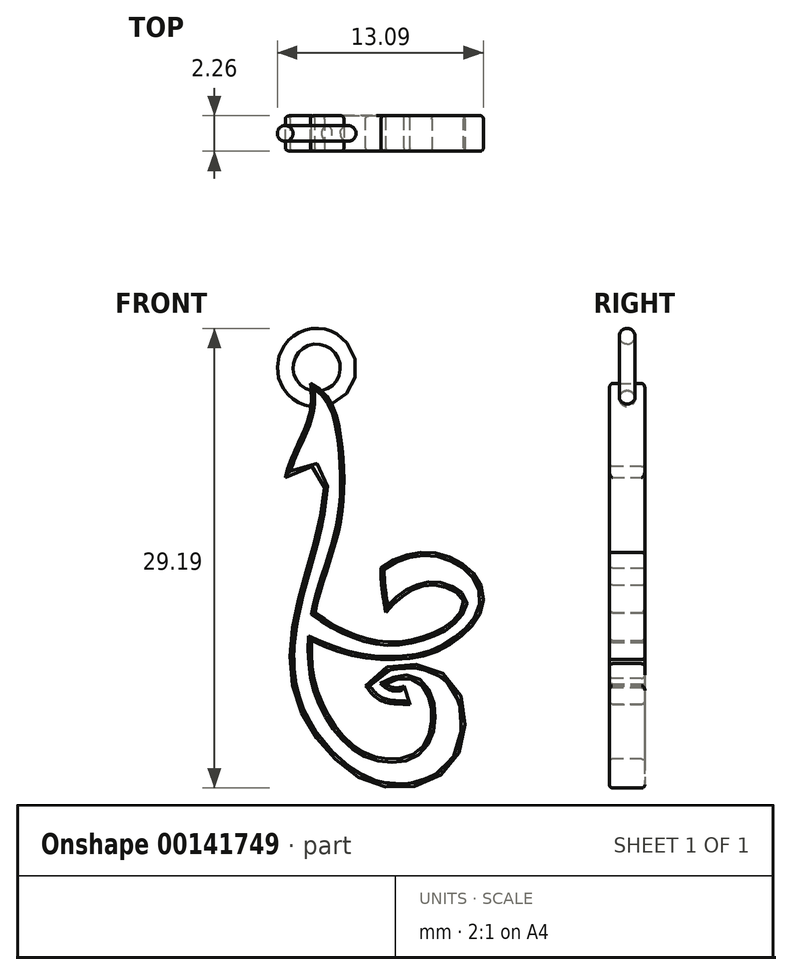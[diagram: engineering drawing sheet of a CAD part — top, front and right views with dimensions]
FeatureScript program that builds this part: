
annotation { "Feature Type Name" : "Feature", "Feature Type Description" : "" }
export const myFeature = defineFeature(function(context is Context, id is Id, definition is map)
    precondition{}
    {
        {
            var Q0;
            Q0=qCreatedBy(makeId("Front.planeOp"),FACE);
            var sketch = newSketch(context, id + "F0", { "sketchPlane" : qUnion([Q0])});
            skLineSegment(sketch, "E0.bottom", {"start": v(-7.5, 0) * mm, "end": v(9.5, 0) * mm, "construction": true});
            skLineSegment(sketch, "E0.top", {"start": v(-7.5, 17) * mm, "end": v(9.5, 17) * mm, "construction": true});
            skLineSegment(sketch, "E0.left", {"start": v(-7.5, 0) * mm, "end": v(-7.5, 17) * mm, "construction": true});
            skLineSegment(sketch, "E0.right", {"start": v(9.5, 0) * mm, "end": v(9.5, 17) * mm, "construction": true});
            skLineSegment(sketch, "E1", {"start": v(0, 0) * mm, "end": v(0, 23.23) * mm, "construction": true});
            skLineSegment(sketch, "E2", {"start": v(2.11, 3.42) * mm, "end": v(1.86, 4.2) * mm});
            skFitSpline(sketch, "E3", {"points": [v(1.86, 4.2) * mm, v(1.1, 4.27) * mm], "startDerivative": vector(-0.68, -0.46) * mm, "endDerivative": vector(-0.68, 0.54) * mm});
            skFitSpline(sketch, "E4", {"points": [v(1.1, 4.27) * mm, v(1.6, 4.48) * mm, v(2.23, 4.46) * mm, v(2.83, 3.93) * mm, v(3.04, 2.91) * mm, v(2.87, 1.98) * mm, v(2.32, 1.32) * mm, v(1.42, 1.1) * mm, v(0.23, 1.34) * mm, v(-0.95, 2.35) * mm, v(-1.8, 3.96) * mm, v(-2.06, 5.52) * mm, v(-1.91, 7.29) * mm, v(-1.38, 9.13) * mm, v(-0.76, 11.56) * mm, v(-0.75, 14.1) * mm, v(-1.06, 15.82) * mm, v(-1.44, 16.5) * mm, v(-2.1, 17) * mm], "startDerivative": vector(23.92, 10.43) * mm, "endDerivative": vector(-24, 9.9) * mm});
            skFitSpline(sketch, "E5", {"points": [v(-1.91, 7.29) * mm, v(-0.55, 6.48) * mm, v(1.22, 6.04) * mm, v(2.68, 6.28) * mm, v(3.76, 6.8) * mm, v(4.4, 7.67) * mm, v(4.1, 8.14) * mm, v(3.43, 8.42) * mm, v(2.66, 8.42) * mm, v(1.7, 7.91) * mm, v(1.1, 7.3) * mm], "startDerivative": vector(12.7, -8.61) * mm, "endDerivative": vector(-6.05, -7.17) * mm});
            skFitSpline(sketch, "E6", {"points": [v(1.1, 7.3) * mm, v(0.9, 9.19) * mm], "startDerivative": vector(-0.46, 2.24) * mm, "endDerivative": vector(0.08, 1.5) * mm});
            skFitSpline(sketch, "E7", {"points": [v(-2.05, 6.11) * mm, v(-0.62, 5.55) * mm, v(0.65, 5.33) * mm, v(2.15, 5.37) * mm, v(3.39, 5.7) * mm, v(4.57, 6.55) * mm, v(5.04, 7.15) * mm, v(5.22, 7.9) * mm, v(4.96, 8.76) * mm, v(3.99, 9.56) * mm, v(2.88, 9.84) * mm, v(1.66, 9.64) * mm, v(0.9, 9.19) * mm], "startDerivative": vector(15.2, -6.57) * mm, "endDerivative": vector(-9.55, -6.77) * mm});
            skFitSpline(sketch, "E8", {"points": [v(-2.1, 17) * mm, v(-2.1, 15.83) * mm, v(-2.63, 14.44) * mm, v(-3.16, 13.02) * mm], "startDerivative": vector(0.45, -3.7) * mm, "endDerivative": vector(-0.8, -3.86) * mm});
            skFitSpline(sketch, "E9", {"points": [v(-3.16, 13.02) * mm, v(-2.25, 13.44) * mm, v(-1.67, 13.4) * mm, v(-1.5, 12.7) * mm, v(-1.85, 10.56) * mm, v(-2.67, 7.58) * mm, v(-2.87, 4.3) * mm, v(-1.73, 1.84) * mm, v(-0.34, 0.5) * mm, v(0.5, 0.07) * mm, v(1.81, -0.13) * mm, v(3.3, 0.32) * mm, v(4.3, 1.6) * mm, v(4.37, 3.39) * mm, v(3.84, 4.47) * mm, v(2.78, 5.03) * mm, v(1.66, 5.11) * mm, v(0.76, 4.78) * mm, v(0.24, 4.2) * mm], "startDerivative": vector(20.67, 12.54) * mm, "endDerivative": vector(-11.13, -14.7) * mm});
            skCircle(sketch, "E10", {"center": v(1.36, 12.15) * mm, "radius": 0.4 * mm, "construction": true});
            skFitSpline(sketch, "E11", {"points": [v(0.24, 4.2) * mm, v(2.11, 3.42) * mm], "startDerivative": vector(1.36, -1.73) * mm, "endDerivative": vector(3.89, 0.05) * mm});
            skSolve(sketch);
        }
        {
            var Q0;
            Q0=qSketchRegion(id+"F0",true);
            extrude(context, id + "F1", {"entities" : qUnion([Q0]), "offsetDistance" : 25 * mm, "depth" : 1.25 * mm, "hasSecondDirection" : true, "secondDirectionOppositeDirection" : true, "secondDirectionDepth" : 0.25 * mm});
        }
        {
            var Q0;
            Q0=makeQuery(id+"F1.opExtrude","SWEPT_BODY",BODY,{"disambiguationData":[OSD([sQuery(id+"F0.wireOp",EDGE,"E2"),sQuery(id+"F0.wireOp",EDGE,"E3"),sQuery(id+"F0.wireOp",EDGE,"E4"),sQuery(id+"F0.wireOp",EDGE,"E5"),sQuery(id+"F0.wireOp",EDGE,"E6"),sQuery(id+"F0.wireOp",EDGE,"E7"),sQuery(id+"F0.wireOp",EDGE,"E8"),sQuery(id+"F0.wireOp",EDGE,"E9"),sQuery(id+"F0.wireOp",EDGE,"E11"),sQuery(id+"F0.wireOp",EDGE,"E4")])]});
            var Q1;
            Q1=sQuery(id+"F0.wireOp",VERTEX,"E8.start");
            transform(context, id + "F2", {"entities" : qUnion([Q0]), "transformType" : TransformType.SCALE_UNIFORMLY, "scale" : 1.5, "scalePoint" : qUnion([Q1]), "makeCopy" : false});
        }
        {
            var Q0;
            Q0=qCreatedBy(makeId("Right.planeOp"),FACE);
            cPlane(context, id + "F3", {"entities" : qUnion([Q0]), "cplaneType" : CPlaneType.OFFSET, "offset" : 1.7 * mm, "oppositeDirection" : true, "width" : 150 * mm, "height" : 150 * mm});
        }
        {
            var Q0;
            Q0=qCreatedBy(id+"F3.planeOp",FACE);
            var sketch = newSketch(context, id + "F4", { "sketchPlane" : qUnion([Q0])});
            skCircle(sketch, "E12", {"center": v(-0.75, 16) * mm, "radius": 0.5 * mm});
            skLineSegment(sketch, "E13", {"start": v(-3.17, 18) * mm, "end": v(2.9, 18) * mm, "construction": true});
            skSolve(sketch);
        }
        {
            var Q0;
            Q0=qSketchRegion(id+"F4",true);
            var Q1;
            Q1=sQuery(id+"F4.wireOp",EDGE,"E13");
            revolve(context, id + "F5", {"operationType" : NewBodyOperationType.ADD, "entities" : qUnion([Q0]), "axis" : qUnion([Q1]), "revolveType" : RevolveType.FULL});
        }
        {
            var Q0;
            Q0=makeQuery(id+"F1.opExtrude","CAP_EDGE",EDGE,{"disambiguationData":[OSD([sQuery(id+"F0.wireOp",EDGE,"E5")])],"isStart":true});
            var Q1;
            Q1=makeQuery(id+"F1.opExtrude","CAP_EDGE",EDGE,{"disambiguationData":[OSD([sQuery(id+"F0.wireOp",EDGE,"E7")])],"isStart":true});
            var Q2;
            Q2=makeQuery(id+"F1.opExtrude","CAP_EDGE",EDGE,{"disambiguationData":[OSD([sQuery(id+"F0.wireOp",EDGE,"E2")])],"isStart":true});
            var Q3;
            Q3=makeQuery(id+"F1.opExtrude","CAP_EDGE",EDGE,{"disambiguationData":[OSD([sQuery(id+"F0.wireOp",EDGE,"E4")])],"isStart":true});
            var Q4;
            Q4=makeQuery(id+"F1.opExtrude","CAP_FACE",FACE,{"disambiguationData":[OSD([sQuery(id+"F0.wireOp",EDGE,"E2"),sQuery(id+"F0.wireOp",EDGE,"E3"),sQuery(id+"F0.wireOp",EDGE,"E4"),sQuery(id+"F0.wireOp",EDGE,"E5"),sQuery(id+"F0.wireOp",EDGE,"E6"),sQuery(id+"F0.wireOp",EDGE,"E7"),sQuery(id+"F0.wireOp",EDGE,"E8"),sQuery(id+"F0.wireOp",EDGE,"E9"),sQuery(id+"F0.wireOp",EDGE,"E11"),sQuery(id+"F0.wireOp",EDGE,"E4")])],"isStart":true});
            var Q5;
            Q5=makeQuery(id+"F1.opExtrude","CAP_FACE",FACE,{"disambiguationData":[OSD([sQuery(id+"F0.wireOp",EDGE,"E2"),sQuery(id+"F0.wireOp",EDGE,"E3"),sQuery(id+"F0.wireOp",EDGE,"E4"),sQuery(id+"F0.wireOp",EDGE,"E5"),sQuery(id+"F0.wireOp",EDGE,"E6"),sQuery(id+"F0.wireOp",EDGE,"E7"),sQuery(id+"F0.wireOp",EDGE,"E8"),sQuery(id+"F0.wireOp",EDGE,"E9"),sQuery(id+"F0.wireOp",EDGE,"E11"),sQuery(id+"F0.wireOp",EDGE,"E4")])],"isStart":false});
            fillet(context, id + "F6", {"entities" : qUnion([Q0, Q1, Q2, Q3, Q4, Q5]), "radius" : 0.2 * mm, "allowEdgeOverflow" : false});
        }
    });
